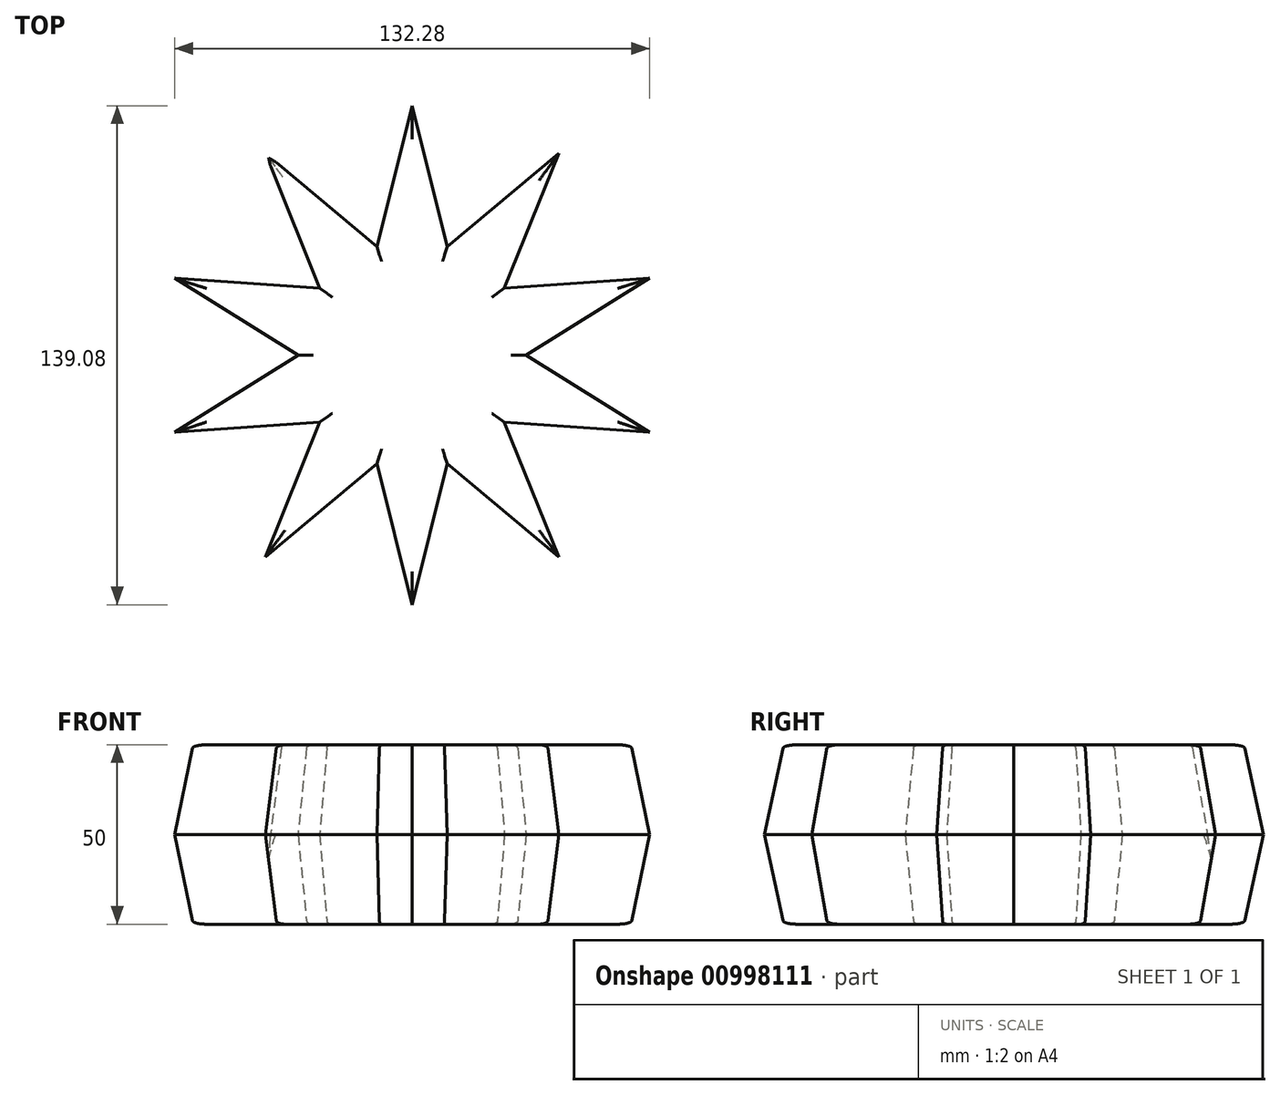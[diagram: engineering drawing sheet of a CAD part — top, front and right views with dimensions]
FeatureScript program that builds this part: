
annotation { "Feature Type Name" : "Feature", "Feature Type Description" : "" }
export const myFeature = defineFeature(function(context is Context, id is Id, definition is map)
    precondition{}
    {
        {
            var Q0;
            Q0=qCreatedBy(makeId("Top.planeOp"),FACE);
            var sketch = newSketch(context, id + "F0", { "sketchPlane" : qUnion([Q0])});
            skCircle(sketch, "E0.cCircle", {"center": v(0, 0) * mm, "radius": 24.14 * mm, "construction": true});
            skLineSegment(sketch, "E0.0", {"start": v(24.14, 10) * mm, "end": v(24.14, -10) * mm});
            skLineSegment(sketch, "E0.1", {"start": v(24.14, -10) * mm, "end": v(10, -24.14) * mm});
            skLineSegment(sketch, "E0.2", {"start": v(10, -24.14) * mm, "end": v(-10, -24.14) * mm});
            skLineSegment(sketch, "E0.3", {"start": v(-10, -24.14) * mm, "end": v(-24.14, -10) * mm});
            skLineSegment(sketch, "E0.4", {"start": v(-24.14, -10) * mm, "end": v(-24.14, 10) * mm});
            skLineSegment(sketch, "E0.5", {"start": v(-24.14, 10) * mm, "end": v(-10, 24.14) * mm});
            skLineSegment(sketch, "E0.6", {"start": v(-10, 24.14) * mm, "end": v(10, 24.14) * mm});
            skLineSegment(sketch, "E0.7", {"start": v(10, 24.14) * mm, "end": v(24.14, 10) * mm});
            skPoint(sketch, "E0.0.midPoint", {"position": v(24.14, 0) * mm});
            skLineSegment(sketch, "E1", {"start": v(-10, 24.14) * mm, "end": v(0, 64.14) * mm});
            skLineSegment(sketch, "E2", {"start": v(0, 64.14) * mm, "end": v(10, 24.14) * mm});
            skLineSegment(sketch, "E3.1.0", {"start": v(-22.28, 13.65) * mm, "end": v(-37.7, 51.9) * mm});
            skLineSegment(sketch, "E3.1.1", {"start": v(-37.7, 51.9) * mm, "end": v(-6.1, 25.4) * mm});
            skLineSegment(sketch, "E3.2.0", {"start": v(-26.05, -2.05) * mm, "end": v(-61, 19.82) * mm});
            skLineSegment(sketch, "E3.2.1", {"start": v(-61, 19.82) * mm, "end": v(-19.87, 16.97) * mm});
            skLineSegment(sketch, "E3.3.0", {"start": v(-19.87, -16.97) * mm, "end": v(-61, -19.82) * mm});
            skLineSegment(sketch, "E3.3.1", {"start": v(-61, -19.82) * mm, "end": v(-26.05, 2.05) * mm});
            skLineSegment(sketch, "E3.4.0", {"start": v(-6.1, -25.4) * mm, "end": v(-37.7, -51.9) * mm});
            skLineSegment(sketch, "E3.4.1", {"start": v(-37.7, -51.9) * mm, "end": v(-22.28, -13.65) * mm});
            skLineSegment(sketch, "E3.5.0", {"start": v(10, -24.14) * mm, "end": v(0, -64.14) * mm});
            skLineSegment(sketch, "E3.5.1", {"start": v(0, -64.14) * mm, "end": v(-10, -24.14) * mm});
            skLineSegment(sketch, "E3.6.0", {"start": v(22.28, -13.65) * mm, "end": v(37.7, -51.9) * mm});
            skLineSegment(sketch, "E3.6.1", {"start": v(37.7, -51.9) * mm, "end": v(6.1, -25.4) * mm});
            skLineSegment(sketch, "E3.7.0", {"start": v(26.05, 2.05) * mm, "end": v(61, -19.82) * mm});
            skLineSegment(sketch, "E3.7.1", {"start": v(61, -19.82) * mm, "end": v(19.87, -16.97) * mm});
            skLineSegment(sketch, "E3.8.0", {"start": v(19.87, 16.97) * mm, "end": v(61, 19.82) * mm});
            skLineSegment(sketch, "E3.8.1", {"start": v(61, 19.82) * mm, "end": v(26.05, -2.05) * mm});
            skLineSegment(sketch, "E3.9.0", {"start": v(6.1, 25.4) * mm, "end": v(37.7, 51.9) * mm});
            skLineSegment(sketch, "E3.9.1", {"start": v(37.7, 51.9) * mm, "end": v(22.28, 13.65) * mm});
            skSolve(sketch);
        }
        {
            var Q0;
            {var subQ13=sQuery(id+"F0.wireOp",EDGE,"E0.3");Q0=makeQuery(id+"F0.imprint","IMPRINT",FACE,{"disambiguationData":[TD([[makeQuery(id+"F0.imprint","IMPRINT",EDGE,{"derivedFrom":subQ13}),1.0]])]});}
            var Q1;
            {var subQ5=sQuery(id+"F0.wireOp",EDGE,"E0.6");Q1=makeQuery(id+"F0.imprint","IMPRINT",FACE,{"disambiguationData":[TD([[makeQuery(id+"F0.imprint","IMPRINT",EDGE,{"derivedFrom":subQ5}),1.0]])]});}
            var Q2;
            Q2=makeQuery(id+"F0.imprint","IMPRINT",FACE,{"disambiguationData":[TD([[makeQuery(id+"F0.imprint","IMPRINT",EDGE,{"derivedFrom":sQuery(id+"F0.wireOp",EDGE,"E0.0")}),1.0]])]});
            var Q3;
            {var subQ4=sQuery(id+"F0.wireOp",EDGE,"E0.2");Q3=makeQuery(id+"F0.imprint","IMPRINT",FACE,{"disambiguationData":[TD([[makeQuery(id+"F0.imprint","IMPRINT",EDGE,{"derivedFrom":subQ4}),1.0]])]});}
            var Q4;
            Q4=makeQuery(id+"F0.imprint","IMPRINT",FACE,{"disambiguationData":[TD([[makeQuery(id+"F0.imprint","IMPRINT",EDGE,{"derivedFrom":sQuery(id+"F0.wireOp",EDGE,"E0.0")}),-1.0]])]});
            extrude(context, id + "F1", {"entities" : qUnion([Q0, Q1, Q2, Q3, Q4]), "depth" : 25 * mm, "offsetDistance" : 25 * mm, "hasDraft" : true, "draftAngle" : 3 * degree});
        }
        {
            var Q0;
            Q0=makeQuery(id+"F1.opExtrude","CAP_FACE",FACE,{"disambiguationData":[OSD([sQuery(id+"F0.wireOp",EDGE,"E1"),sQuery(id+"F0.wireOp",EDGE,"E2"),sQuery(id+"F0.wireOp",EDGE,"E3.1.0"),sQuery(id+"F0.wireOp",EDGE,"E3.1.1"),sQuery(id+"F0.wireOp",EDGE,"E3.2.0"),sQuery(id+"F0.wireOp",EDGE,"E3.2.1"),sQuery(id+"F0.wireOp",EDGE,"E3.3.0"),sQuery(id+"F0.wireOp",EDGE,"E3.3.1"),sQuery(id+"F0.wireOp",EDGE,"E3.4.0"),sQuery(id+"F0.wireOp",EDGE,"E3.4.1"),sQuery(id+"F0.wireOp",EDGE,"E3.5.0"),sQuery(id+"F0.wireOp",EDGE,"E3.5.1"),sQuery(id+"F0.wireOp",EDGE,"E3.6.0"),sQuery(id+"F0.wireOp",EDGE,"E3.6.1"),sQuery(id+"F0.wireOp",EDGE,"E3.7.0"),sQuery(id+"F0.wireOp",EDGE,"E3.7.1"),sQuery(id+"F0.wireOp",EDGE,"E3.8.0"),sQuery(id+"F0.wireOp",EDGE,"E3.8.1"),sQuery(id+"F0.wireOp",EDGE,"E3.9.0"),sQuery(id+"F0.wireOp",EDGE,"E3.9.1")])],"isStart":false});
            var sketch = newSketch(context, id + "F2", { "sketchPlane" : qUnion([Q0])});
            skLineSegment(sketch, "E4.0", {"start": v(-25.72, 18.69) * mm, "end": v(-40.88, 56.26) * mm});
            skLineSegment(sketch, "E4.1", {"start": v(-40.88, 56.26) * mm, "end": v(-9.83, 30.24) * mm});
            skLineSegment(sketch, "E5.0", {"start": v(-66.14, 21.5) * mm, "end": v(-25.72, 18.69) * mm});
            skLineSegment(sketch, "E5.1", {"start": v(-31.8, 0) * mm, "end": v(-66.14, 21.5) * mm});
            skLineSegment(sketch, "E5.2", {"start": v(-66.14, -21.5) * mm, "end": v(-31.8, 0) * mm});
            skLineSegment(sketch, "E5.3", {"start": v(-25.72, -18.69) * mm, "end": v(-66.14, -21.5) * mm});
            skLineSegment(sketch, "E5.4", {"start": v(-40.88, -56.26) * mm, "end": v(-25.72, -18.69) * mm});
            skLineSegment(sketch, "E5.5", {"start": v(-9.83, -30.24) * mm, "end": v(-40.88, -56.26) * mm});
            skLineSegment(sketch, "E5.6", {"start": v(0, -69.54) * mm, "end": v(-9.83, -30.24) * mm});
            skLineSegment(sketch, "E5.7", {"start": v(9.83, -30.24) * mm, "end": v(0, -69.54) * mm});
            skLineSegment(sketch, "E5.8", {"start": v(40.88, -56.26) * mm, "end": v(9.83, -30.24) * mm});
            skLineSegment(sketch, "E5.9", {"start": v(25.72, -18.69) * mm, "end": v(40.88, -56.26) * mm});
            skLineSegment(sketch, "E5.10", {"start": v(66.14, -21.5) * mm, "end": v(25.72, -18.69) * mm});
            skLineSegment(sketch, "E5.11", {"start": v(31.8, 0) * mm, "end": v(66.14, -21.5) * mm});
            skLineSegment(sketch, "E5.12", {"start": v(66.14, 21.5) * mm, "end": v(31.8, 0) * mm});
            skLineSegment(sketch, "E5.13", {"start": v(25.72, 18.69) * mm, "end": v(66.14, 21.5) * mm});
            skLineSegment(sketch, "E5.14", {"start": v(40.88, 56.26) * mm, "end": v(25.72, 18.69) * mm});
            skLineSegment(sketch, "E5.15", {"start": v(9.83, 30.24) * mm, "end": v(40.88, 56.26) * mm});
            skLineSegment(sketch, "E5.16", {"start": v(0, 69.54) * mm, "end": v(9.83, 30.24) * mm});
            skLineSegment(sketch, "E5.17", {"start": v(-9.83, 30.24) * mm, "end": v(0, 69.54) * mm});
            skSolve(sketch);
        }
        {
            var Q0;
            Q0 = qSketchRegion(id + "F2", true);
            extrude(context, id + "F3", {"entities" : qUnion([Q0]), "operationType" : NewBodyOperationType.ADD, "depth" : 25 * mm, "offsetDistance" : 25 * mm, "hasDraft" : true, "draftAngle" : 3 * degree, "draftPullDirection" : true});
        }
        {
            var Q0;
            Q0=makeQuery(id+"F3.opExtrude","CAP_FACE",FACE,{"disambiguationData":[OSD([sQuery(id+"F2.wireOp",EDGE,"E4.0"),sQuery(id+"F2.wireOp",EDGE,"E4.1"),sQuery(id+"F2.wireOp",EDGE,"E5.0"),sQuery(id+"F2.wireOp",EDGE,"E5.1"),sQuery(id+"F2.wireOp",EDGE,"E5.2"),sQuery(id+"F2.wireOp",EDGE,"E5.3"),sQuery(id+"F2.wireOp",EDGE,"E5.4"),sQuery(id+"F2.wireOp",EDGE,"E5.5"),sQuery(id+"F2.wireOp",EDGE,"E5.6"),sQuery(id+"F2.wireOp",EDGE,"E5.7"),sQuery(id+"F2.wireOp",EDGE,"E5.8"),sQuery(id+"F2.wireOp",EDGE,"E5.9"),sQuery(id+"F2.wireOp",EDGE,"E5.10"),sQuery(id+"F2.wireOp",EDGE,"E5.11"),sQuery(id+"F2.wireOp",EDGE,"E5.12"),sQuery(id+"F2.wireOp",EDGE,"E5.13"),sQuery(id+"F2.wireOp",EDGE,"E5.14"),sQuery(id+"F2.wireOp",EDGE,"E5.15"),sQuery(id+"F2.wireOp",EDGE,"E5.16"),sQuery(id+"F2.wireOp",EDGE,"E5.17")])],"isStart":false});
            var Q1;
            Q1=makeQuery(id+"F1.opExtrude","CAP_FACE",FACE,{"disambiguationData":[OSD([sQuery(id+"F0.wireOp",EDGE,"E1"),sQuery(id+"F0.wireOp",EDGE,"E2"),sQuery(id+"F0.wireOp",EDGE,"E3.1.0"),sQuery(id+"F0.wireOp",EDGE,"E3.1.1"),sQuery(id+"F0.wireOp",EDGE,"E3.2.0"),sQuery(id+"F0.wireOp",EDGE,"E3.2.1"),sQuery(id+"F0.wireOp",EDGE,"E3.3.0"),sQuery(id+"F0.wireOp",EDGE,"E3.3.1"),sQuery(id+"F0.wireOp",EDGE,"E3.4.0"),sQuery(id+"F0.wireOp",EDGE,"E3.4.1"),sQuery(id+"F0.wireOp",EDGE,"E3.5.0"),sQuery(id+"F0.wireOp",EDGE,"E3.5.1"),sQuery(id+"F0.wireOp",EDGE,"E3.6.0"),sQuery(id+"F0.wireOp",EDGE,"E3.6.1"),sQuery(id+"F0.wireOp",EDGE,"E3.7.0"),sQuery(id+"F0.wireOp",EDGE,"E3.7.1"),sQuery(id+"F0.wireOp",EDGE,"E3.8.0"),sQuery(id+"F0.wireOp",EDGE,"E3.8.1"),sQuery(id+"F0.wireOp",EDGE,"E3.9.0"),sQuery(id+"F0.wireOp",EDGE,"E3.9.1")])],"isStart":true});
            var Q2;
            Q2=makeQuery(id+"F3.opExtrude","SWEPT_EDGE",EDGE,{"disambiguationData":[OSD([sQuery(id+"F2.wireOp",EDGE,"E4.0"),sQuery(id+"F2.wireOp",EDGE,"E4.1")])]});
            fillet(context, id + "F4", {"entities" : qUnion([Q0, Q1, Q2]), "radius" : 1 * mm, "tangentPropagation" : true, "allowEdgeOverflow" : false});
        }
    });
